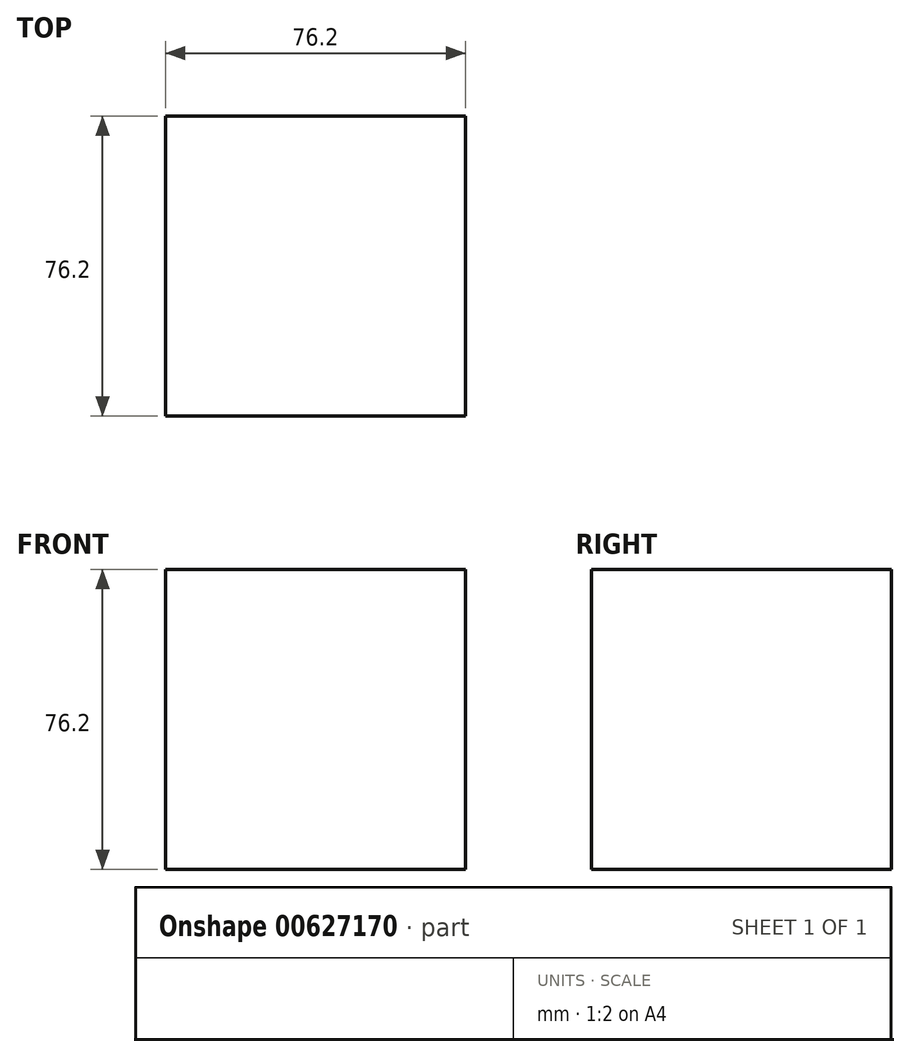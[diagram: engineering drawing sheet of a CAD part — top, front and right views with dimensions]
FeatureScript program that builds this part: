
annotation { "Feature Type Name" : "Feature", "Feature Type Description" : "" }
export const myFeature = defineFeature(function(context is Context, id is Id, definition is map)
    precondition{}
    {
        {
            var Q0;
            Q0=qCreatedBy(makeId("Front.planeOp"),FACE);
            var sketch = newSketch(context, id + "F0", { "sketchPlane" : qUnion([Q0])});
            skLineSegment(sketch, "E0.bottom", {"start": v(0, 0) * mm, "end": v(-76.2, 0) * mm});
            skLineSegment(sketch, "E0.top", {"start": v(0, 76.2) * mm, "end": v(-76.2, 76.2) * mm});
            skLineSegment(sketch, "E0.left", {"start": v(0, 0) * mm, "end": v(0, 76.2) * mm});
            skLineSegment(sketch, "E0.right", {"start": v(-76.2, 0) * mm, "end": v(-76.2, 76.2) * mm});
            skSolve(sketch);
        }
        {
            var Q0;
            Q0 = qSketchRegion(id + "F0", true);
            extrude(context, id + "F1", {"entities" : qUnion([Q0]), "depth" : 76.2 * mm, "offsetDistance" : 25.4 * mm});
        }
    });
